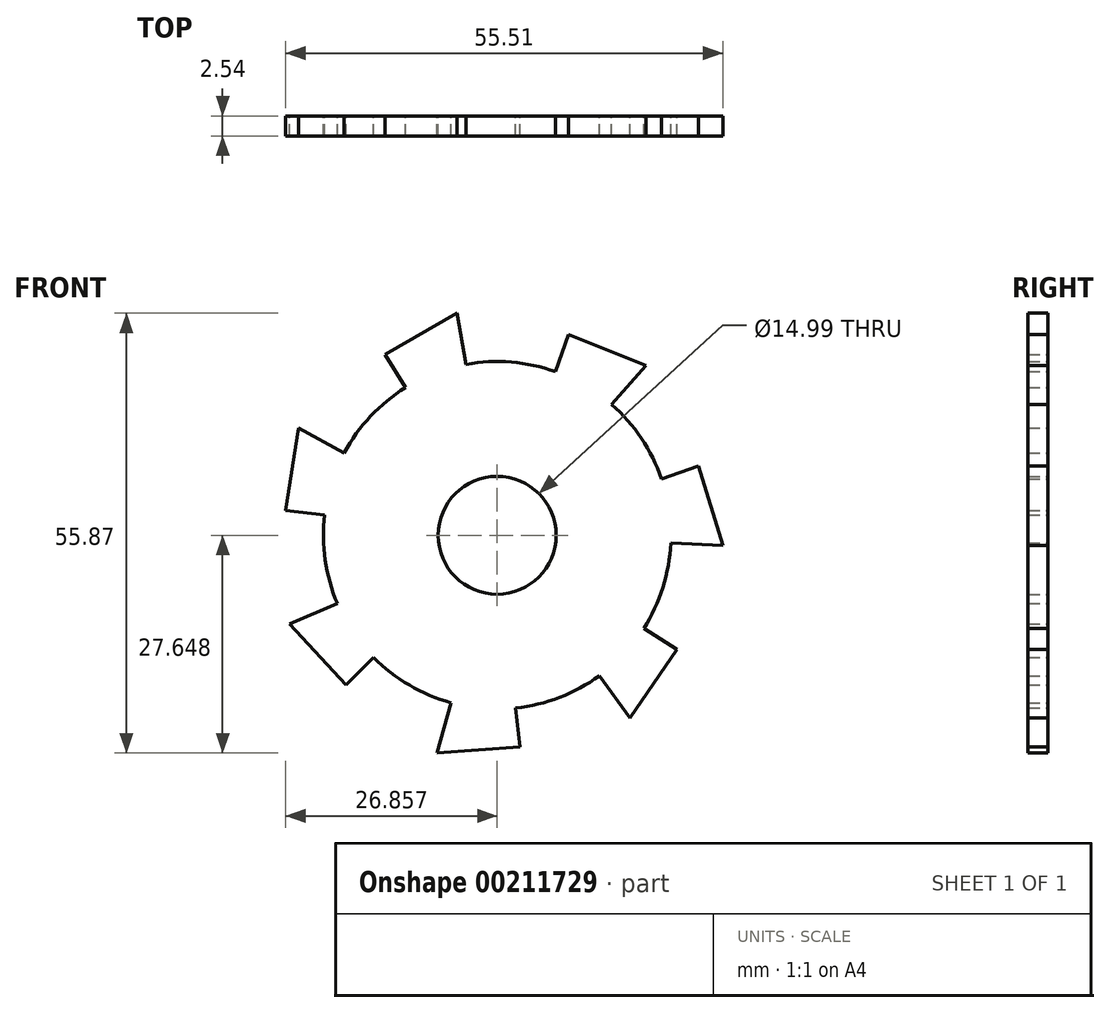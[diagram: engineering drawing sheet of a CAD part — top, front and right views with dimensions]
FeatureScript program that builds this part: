
annotation { "Feature Type Name" : "Feature", "Feature Type Description" : "" }
export const myFeature = defineFeature(function(context is Context, id is Id, definition is map)
    precondition{}
    {
        {
            var Q0;
            Q0=qCreatedBy(makeId("Front.planeOp"),FACE);
            var sketch = newSketch(context, id + "F0", { "sketchPlane" : qUnion([Q0])});
            skLineSegment(sketch, "E0", {"start": v(0, 0) * mm, "end": v(26.04, 0) * mm});
            skLineSegment(sketch, "E1", {"start": v(26.03, 0) * mm, "end": v(42.27, 20.35) * mm});
            skLineSegment(sketch, "E2", {"start": v(26.04, 0) * mm, "end": v(33.02, 0) * mm});
            skLineSegment(sketch, "E3", {"start": v(42.27, 20.35) * mm, "end": v(36.47, 45.74) * mm});
            skLineSegment(sketch, "E4", {"start": v(42.27, 20.35) * mm, "end": v(46.62, 25.82) * mm});
            skLineSegment(sketch, "E5", {"start": v(36.47, 45.74) * mm, "end": v(13.02, 57.03) * mm});
            skLineSegment(sketch, "E6", {"start": v(13.02, 57.03) * mm, "end": v(-10.44, 45.74) * mm});
            skLineSegment(sketch, "E7", {"start": v(0, 0) * mm, "end": v(-5.08, 0) * mm});
            skLineSegment(sketch, "E8", {"start": v(26.04, 0) * mm, "end": v(22.87, -3.97) * mm});
            skLineSegment(sketch, "E9", {"start": v(42.27, 20.35) * mm, "end": v(43.4, 15.4) * mm});
            skLineSegment(sketch, "E10", {"start": v(36.47, 45.74) * mm, "end": v(34.92, 52.55) * mm});
            skLineSegment(sketch, "E11", {"start": v(36.47, 45.74) * mm, "end": v(41.05, 43.53) * mm});
            skLineSegment(sketch, "E12", {"start": v(13.02, 57.03) * mm, "end": v(6.72, 60.06) * mm});
            skLineSegment(sketch, "E13", {"start": v(13.02, 57.03) * mm, "end": v(17.6, 59.24) * mm});
            skLineSegment(sketch, "E14", {"start": v(-10.44, 45.74) * mm, "end": v(-16.73, 42.7) * mm});
            skLineSegment(sketch, "E15", {"start": v(-16.23, 20.35) * mm, "end": v(0, 0) * mm});
            skLineSegment(sketch, "E16", {"start": v(-10.44, 45.74) * mm, "end": v(-16.23, 20.35) * mm});
            skLineSegment(sketch, "E17", {"start": v(-10.44, 45.74) * mm, "end": v(-9.3, 50.69) * mm});
            skLineSegment(sketch, "E18", {"start": v(-16.23, 20.35) * mm, "end": v(-16.23, 13.22) * mm});
            skLineSegment(sketch, "E19", {"start": v(-16.23, 20.35) * mm, "end": v(-19.4, 24.33) * mm});
            skLineSegment(sketch, "E20", {"start": v(0, 0) * mm, "end": v(4.36, -5.46) * mm});
            skPoint(sketch, "E21", {"position": v(3.43, 0) * mm});
            skPoint(sketch, "E22", {"position": v(13.97, 0) * mm});
            skPoint(sketch, "E23", {"position": v(28.17, 2.68) * mm});
            skPoint(sketch, "E24", {"position": v(34.75, 10.92) * mm});
            skPoint(sketch, "E25", {"position": v(41.5, 23.7) * mm});
            skPoint(sketch, "E26", {"position": v(39.16, 33.97) * mm});
            skPoint(sketch, "E27", {"position": v(33.38, 47.23) * mm});
            skPoint(sketch, "E28", {"position": v(23.89, 51.8) * mm});
            skPoint(sketch, "E29", {"position": v(9.93, 55.55) * mm});
            skPoint(sketch, "E30", {"position": v(0.43, 50.97) * mm});
            skPoint(sketch, "E31", {"position": v(-11.2, 42.4) * mm});
            skPoint(sketch, "E32", {"position": v(-13.55, 32.12) * mm});
            skPoint(sketch, "E33", {"position": v(-14.1, 17.67) * mm});
            skPoint(sketch, "E34", {"position": v(-7.52, 9.43) * mm});
            skArc(sketch, "E35.cCircle", {"start": v(93.18, 18.18) * mm, "mid": v(93.11, 17.7) * mm, "end": v(93.05, 17.23) * mm, "construction": true});
            skLineSegment(sketch, "E35.0", {"start": v(93.04, 17.24) * mm, "end": v(94.64, 27.65) * mm});
            skLineSegment(sketch, "E35.1", {"start": v(105.63, 37.04) * mm, "end": v(114.78, 42.28) * mm});
            skLineSegment(sketch, "E35.2", {"start": v(128.97, 39.54) * mm, "end": v(138.77, 35.65) * mm});
            skLineSegment(sketch, "E35.3", {"start": v(145.48, 22.85) * mm, "end": v(148.55, 12.77) * mm});
            skLineSegment(sketch, "E35.4", {"start": v(142.72, -0.46) * mm, "end": v(136.75, -9.15) * mm});
            skLineSegment(sketch, "E35.5", {"start": v(122.78, -12.84) * mm, "end": v(112.26, -13.59) * mm});
            skLineSegment(sketch, "E35.6", {"start": v(100.67, -4.96) * mm, "end": v(93.52, 2.8) * mm});
            skPoint(sketch, "E36", {"position": v(112.26, -13.59) * mm});
            skPoint(sketch, "E37", {"position": v(122.78, -12.84) * mm});
            skPoint(sketch, "E38", {"position": v(136.75, -9.15) * mm});
            skPoint(sketch, "E39", {"position": v(142.72, -0.46) * mm});
            skPoint(sketch, "E40", {"position": v(148.55, 12.77) * mm});
            skPoint(sketch, "E41", {"position": v(145.48, 22.85) * mm});
            skPoint(sketch, "E42", {"position": v(138.77, 35.65) * mm});
            skPoint(sketch, "E43", {"position": v(114.78, 42.28) * mm});
            skPoint(sketch, "E44", {"position": v(105.63, 37.04) * mm});
            skPoint(sketch, "E45", {"position": v(94.64, 27.65) * mm});
            skPoint(sketch, "E46", {"position": v(93.04, 17.24) * mm});
            skPoint(sketch, "E47", {"position": v(93.52, 2.8) * mm});
            skPoint(sketch, "E48", {"position": v(100.67, -4.96) * mm});
            skPoint(sketch, "E49", {"position": v(128.97, 39.54) * mm});
            skLineSegment(sketch, "E50", {"start": v(119.9, 14.06) * mm, "end": v(114.78, 42.28) * mm});
            skLineSegment(sketch, "E51", {"start": v(119.9, 14.06) * mm, "end": v(105.63, 37.04) * mm});
            skLineSegment(sketch, "E52", {"start": v(119.9, 14.06) * mm, "end": v(94.64, 27.65) * mm});
            skLineSegment(sketch, "E53", {"start": v(119.9, 14.06) * mm, "end": v(93.04, 17.24) * mm});
            skLineSegment(sketch, "E54", {"start": v(119.9, 14.06) * mm, "end": v(93.52, 2.8) * mm});
            skLineSegment(sketch, "E55", {"start": v(119.9, 14.06) * mm, "end": v(100.67, -4.96) * mm});
            skLineSegment(sketch, "E56", {"start": v(119.9, 14.06) * mm, "end": v(112.26, -13.59) * mm});
            skLineSegment(sketch, "E57", {"start": v(119.9, 14.06) * mm, "end": v(122.78, -12.84) * mm});
            skLineSegment(sketch, "E58", {"start": v(119.9, 14.06) * mm, "end": v(136.75, -9.15) * mm});
            skLineSegment(sketch, "E59", {"start": v(119.9, 14.06) * mm, "end": v(142.72, -0.46) * mm});
            skLineSegment(sketch, "E60", {"start": v(119.9, 14.06) * mm, "end": v(148.55, 12.77) * mm});
            skLineSegment(sketch, "E61", {"start": v(119.9, 14.06) * mm, "end": v(145.48, 22.85) * mm});
            skLineSegment(sketch, "E62", {"start": v(119.9, 14.06) * mm, "end": v(138.77, 35.65) * mm});
            skPoint(sketch, "E63.orphan", {"position": v(95.17, 31.04) * mm});
            skLineSegment(sketch, "E64", {"start": v(128.97, 39.54) * mm, "end": v(119.9, 14.06) * mm});
            skPoint(sketch, "E65.orphan", {"position": v(117.76, 43.98) * mm});
            skArc(sketch, "E66.trimOffspring", {"start": v(106.46, 37.51) * mm, "mid": v(106.05, 37.27) * mm, "end": v(105.64, 37.03) * mm, "construction": true});
            skPoint(sketch, "E67.orphan", {"position": v(141.96, 34.4) * mm});
            skArc(sketch, "E68.trimOffspring", {"start": v(129.86, 39.19) * mm, "mid": v(129.41, 39.36) * mm, "end": v(128.97, 39.52) * mm, "construction": true});
            skPoint(sketch, "E69.orphan", {"position": v(149.55, 9.49) * mm});
            skArc(sketch, "E70.trimOffspring", {"start": v(145.75, 21.94) * mm, "mid": v(145.61, 22.4) * mm, "end": v(145.46, 22.84) * mm, "construction": true});
            skPoint(sketch, "E71.orphan", {"position": v(134.81, -11.97) * mm});
            skArc(sketch, "E72.trimOffspring", {"start": v(142.18, -1.24) * mm, "mid": v(142.45, -0.85) * mm, "end": v(142.7, -0.45) * mm, "construction": true});
            skArc(sketch, "E73.trimOffspring", {"start": v(121.83, -12.9) * mm, "mid": v(122.3, -12.87) * mm, "end": v(122.77, -12.82) * mm, "construction": true});
            skPoint(sketch, "E74.orphan", {"position": v(108.84, -13.83) * mm});
            skPoint(sketch, "E75.orphan", {"position": v(91.2, 5.31) * mm});
            skArc(sketch, "E76.trimOffspring", {"start": v(100.02, -4.26) * mm, "mid": v(100.35, -4.6) * mm, "end": v(100.68, -4.95) * mm, "construction": true});
            skCircle(sketch, "E77", {"center": v(119.9, 14.06) * mm, "radius": 22.07 * mm});
            skCircle(sketch, "E78", {"center": v(119.9, 14.06) * mm, "radius": 7.5 * mm});
            skSolve(sketch);
        }
        {
            var Q0;
            {var subQ0=sQuery(id+"F0.wireOp",EDGE,"E77");var subQ1=sQuery(id+"F0.wireOp",EDGE,"E52");var subQ2=makeQuery(id+"F0.imprint","INTERSECT",VERTEX,{"derivedFrom":[subQ1,subQ0]});Q0=makeQuery(id+"F0.imprint","IMPRINT",FACE,{"disambiguationData":[TD([[makeQuery(id+"F0.imprint","IMPRINT",EDGE,{"disambiguationData":[TD([[subQ2,1.0]])],"derivedFrom":subQ1}),1.0]])]});}
            var Q1;
            {var subQ0=sQuery(id+"F0.wireOp",EDGE,"E35.0");Q1=makeQuery(id+"F0.imprint","IMPRINT",FACE,{"disambiguationData":[TD([[makeQuery(id+"F0.imprint","IMPRINT",EDGE,{"derivedFrom":subQ0}),-1.0]])]});}
            var Q2;
            {var subQ0=sQuery(id+"F0.wireOp",EDGE,"E77");var subQ1=sQuery(id+"F0.wireOp",EDGE,"E51");var subQ2=makeQuery(id+"F0.imprint","INTERSECT",VERTEX,{"derivedFrom":[subQ1,subQ0]});Q2=makeQuery(id+"F0.imprint","IMPRINT",FACE,{"disambiguationData":[TD([[makeQuery(id+"F0.imprint","IMPRINT",EDGE,{"disambiguationData":[TD([[subQ2,1.0]])],"derivedFrom":subQ1}),1.0]])]});}
            var Q3;
            {var subQ0=sQuery(id+"F0.wireOp",EDGE,"E35.1");Q3=makeQuery(id+"F0.imprint","IMPRINT",FACE,{"disambiguationData":[TD([[makeQuery(id+"F0.imprint","IMPRINT",EDGE,{"derivedFrom":subQ0}),-1.0]])]});}
            var Q4;
            {var subQ0=sQuery(id+"F0.wireOp",EDGE,"E77");var subQ1=sQuery(id+"F0.wireOp",EDGE,"E50");var subQ2=makeQuery(id+"F0.imprint","INTERSECT",VERTEX,{"derivedFrom":[subQ1,subQ0]});Q4=makeQuery(id+"F0.imprint","IMPRINT",FACE,{"disambiguationData":[TD([[makeQuery(id+"F0.imprint","IMPRINT",EDGE,{"disambiguationData":[TD([[subQ2,1.0]])],"derivedFrom":subQ1}),1.0]])]});}
            var Q5;
            {var subQ0=sQuery(id+"F0.wireOp",EDGE,"E77");var subQ1=sQuery(id+"F0.wireOp",EDGE,"E50");var subQ2=makeQuery(id+"F0.imprint","INTERSECT",VERTEX,{"derivedFrom":[subQ1,subQ0]});Q5=makeQuery(id+"F0.imprint","IMPRINT",FACE,{"disambiguationData":[TD([[makeQuery(id+"F0.imprint","IMPRINT",EDGE,{"disambiguationData":[TD([[subQ2,1.0]])],"derivedFrom":subQ1}),-1.0]])]});}
            var Q6;
            {var subQ0=sQuery(id+"F0.wireOp",EDGE,"E35.2");Q6=makeQuery(id+"F0.imprint","IMPRINT",FACE,{"disambiguationData":[TD([[makeQuery(id+"F0.imprint","IMPRINT",EDGE,{"derivedFrom":subQ0}),-1.0]])]});}
            var Q7;
            {var subQ0=sQuery(id+"F0.wireOp",EDGE,"E77");var subQ1=sQuery(id+"F0.wireOp",EDGE,"E60");var subQ2=makeQuery(id+"F0.imprint","INTERSECT",VERTEX,{"derivedFrom":[subQ1,subQ0]});Q7=makeQuery(id+"F0.imprint","IMPRINT",FACE,{"disambiguationData":[TD([[makeQuery(id+"F0.imprint","IMPRINT",EDGE,{"disambiguationData":[TD([[subQ2,1.0]])],"derivedFrom":subQ1}),1.0]])]});}
            var Q8;
            {var subQ0=sQuery(id+"F0.wireOp",EDGE,"E35.3");Q8=makeQuery(id+"F0.imprint","IMPRINT",FACE,{"disambiguationData":[TD([[makeQuery(id+"F0.imprint","IMPRINT",EDGE,{"derivedFrom":subQ0}),-1.0]])]});}
            var Q9;
            {var subQ0=sQuery(id+"F0.wireOp",EDGE,"E77");var subQ1=sQuery(id+"F0.wireOp",EDGE,"E61");var subQ2=makeQuery(id+"F0.imprint","INTERSECT",VERTEX,{"derivedFrom":[subQ1,subQ0]});Q9=makeQuery(id+"F0.imprint","IMPRINT",FACE,{"disambiguationData":[TD([[makeQuery(id+"F0.imprint","IMPRINT",EDGE,{"disambiguationData":[TD([[subQ2,1.0]])],"derivedFrom":subQ1}),1.0]])]});}
            var Q10;
            {var subQ0=sQuery(id+"F0.wireOp",EDGE,"E77");var subQ1=sQuery(id+"F0.wireOp",EDGE,"E59");var subQ2=makeQuery(id+"F0.imprint","INTERSECT",VERTEX,{"derivedFrom":[subQ1,subQ0]});Q10=makeQuery(id+"F0.imprint","IMPRINT",FACE,{"disambiguationData":[TD([[makeQuery(id+"F0.imprint","IMPRINT",EDGE,{"disambiguationData":[TD([[subQ2,1.0]])],"derivedFrom":subQ1}),1.0]])]});}
            var Q11;
            {var subQ0=sQuery(id+"F0.wireOp",EDGE,"E35.4");Q11=makeQuery(id+"F0.imprint","IMPRINT",FACE,{"disambiguationData":[TD([[makeQuery(id+"F0.imprint","IMPRINT",EDGE,{"derivedFrom":subQ0}),-1.0]])]});}
            var Q12;
            {var subQ0=sQuery(id+"F0.wireOp",EDGE,"E77");var subQ1=sQuery(id+"F0.wireOp",EDGE,"E58");var subQ2=makeQuery(id+"F0.imprint","INTERSECT",VERTEX,{"derivedFrom":[subQ1,subQ0]});Q12=makeQuery(id+"F0.imprint","IMPRINT",FACE,{"disambiguationData":[TD([[makeQuery(id+"F0.imprint","IMPRINT",EDGE,{"disambiguationData":[TD([[subQ2,1.0]])],"derivedFrom":subQ1}),1.0]])]});}
            var Q13;
            {var subQ0=sQuery(id+"F0.wireOp",EDGE,"E77");var subQ1=sQuery(id+"F0.wireOp",EDGE,"E57");var subQ2=makeQuery(id+"F0.imprint","INTERSECT",VERTEX,{"derivedFrom":[subQ1,subQ0]});Q13=makeQuery(id+"F0.imprint","IMPRINT",FACE,{"disambiguationData":[TD([[makeQuery(id+"F0.imprint","IMPRINT",EDGE,{"disambiguationData":[TD([[subQ2,1.0]])],"derivedFrom":subQ1}),1.0]])]});}
            var Q14;
            {var subQ0=sQuery(id+"F0.wireOp",EDGE,"E35.5");Q14=makeQuery(id+"F0.imprint","IMPRINT",FACE,{"disambiguationData":[TD([[makeQuery(id+"F0.imprint","IMPRINT",EDGE,{"derivedFrom":subQ0}),-1.0]])]});}
            var Q15;
            {var subQ0=sQuery(id+"F0.wireOp",EDGE,"E77");var subQ1=sQuery(id+"F0.wireOp",EDGE,"E56");var subQ2=makeQuery(id+"F0.imprint","INTERSECT",VERTEX,{"derivedFrom":[subQ1,subQ0]});Q15=makeQuery(id+"F0.imprint","IMPRINT",FACE,{"disambiguationData":[TD([[makeQuery(id+"F0.imprint","IMPRINT",EDGE,{"disambiguationData":[TD([[subQ2,1.0]])],"derivedFrom":subQ1}),1.0]])]});}
            var Q16;
            {var subQ0=sQuery(id+"F0.wireOp",EDGE,"E77");var subQ1=sQuery(id+"F0.wireOp",EDGE,"E55");var subQ2=makeQuery(id+"F0.imprint","INTERSECT",VERTEX,{"derivedFrom":[subQ1,subQ0]});Q16=makeQuery(id+"F0.imprint","IMPRINT",FACE,{"disambiguationData":[TD([[makeQuery(id+"F0.imprint","IMPRINT",EDGE,{"disambiguationData":[TD([[subQ2,1.0]])],"derivedFrom":subQ1}),1.0]])]});}
            var Q17;
            {var subQ0=sQuery(id+"F0.wireOp",EDGE,"E77");var subQ1=sQuery(id+"F0.wireOp",EDGE,"E54");var subQ2=makeQuery(id+"F0.imprint","INTERSECT",VERTEX,{"derivedFrom":[subQ1,subQ0]});Q17=makeQuery(id+"F0.imprint","IMPRINT",FACE,{"disambiguationData":[TD([[makeQuery(id+"F0.imprint","IMPRINT",EDGE,{"disambiguationData":[TD([[subQ2,1.0]])],"derivedFrom":subQ1}),1.0]])]});}
            var Q18;
            {var subQ0=sQuery(id+"F0.wireOp",EDGE,"E35.6");Q18=makeQuery(id+"F0.imprint","IMPRINT",FACE,{"disambiguationData":[TD([[makeQuery(id+"F0.imprint","IMPRINT",EDGE,{"derivedFrom":subQ0}),-1.0]])]});}
            var Q19;
            {var subQ0=sQuery(id+"F0.wireOp",EDGE,"E77");var subQ1=sQuery(id+"F0.wireOp",EDGE,"E53");var subQ2=makeQuery(id+"F0.imprint","INTERSECT",VERTEX,{"derivedFrom":[subQ1,subQ0]});Q19=makeQuery(id+"F0.imprint","IMPRINT",FACE,{"disambiguationData":[TD([[makeQuery(id+"F0.imprint","IMPRINT",EDGE,{"disambiguationData":[TD([[subQ2,1.0]])],"derivedFrom":subQ1}),1.0]])]});}
            var Q20;
            {var subQ0=sQuery(id+"F0.wireOp",EDGE,"E77");var subQ1=sQuery(id+"F0.wireOp",EDGE,"E62");var subQ2=makeQuery(id+"F0.imprint","INTERSECT",VERTEX,{"derivedFrom":[subQ1,subQ0]});Q20=makeQuery(id+"F0.imprint","IMPRINT",FACE,{"disambiguationData":[TD([[makeQuery(id+"F0.imprint","IMPRINT",EDGE,{"disambiguationData":[TD([[subQ2,1.0]])],"derivedFrom":subQ1}),1.0]])]});}
            extrude(context, id + "F1", {"entities" : qUnion([Q0, Q1, Q2, Q3, Q4, Q5, Q6, Q7, Q8, Q9, Q10, Q11, Q12, Q13, Q14, Q15, Q16, Q17, Q18, Q19, Q20]), "depth" : 2.54 * mm});
        }
    });
